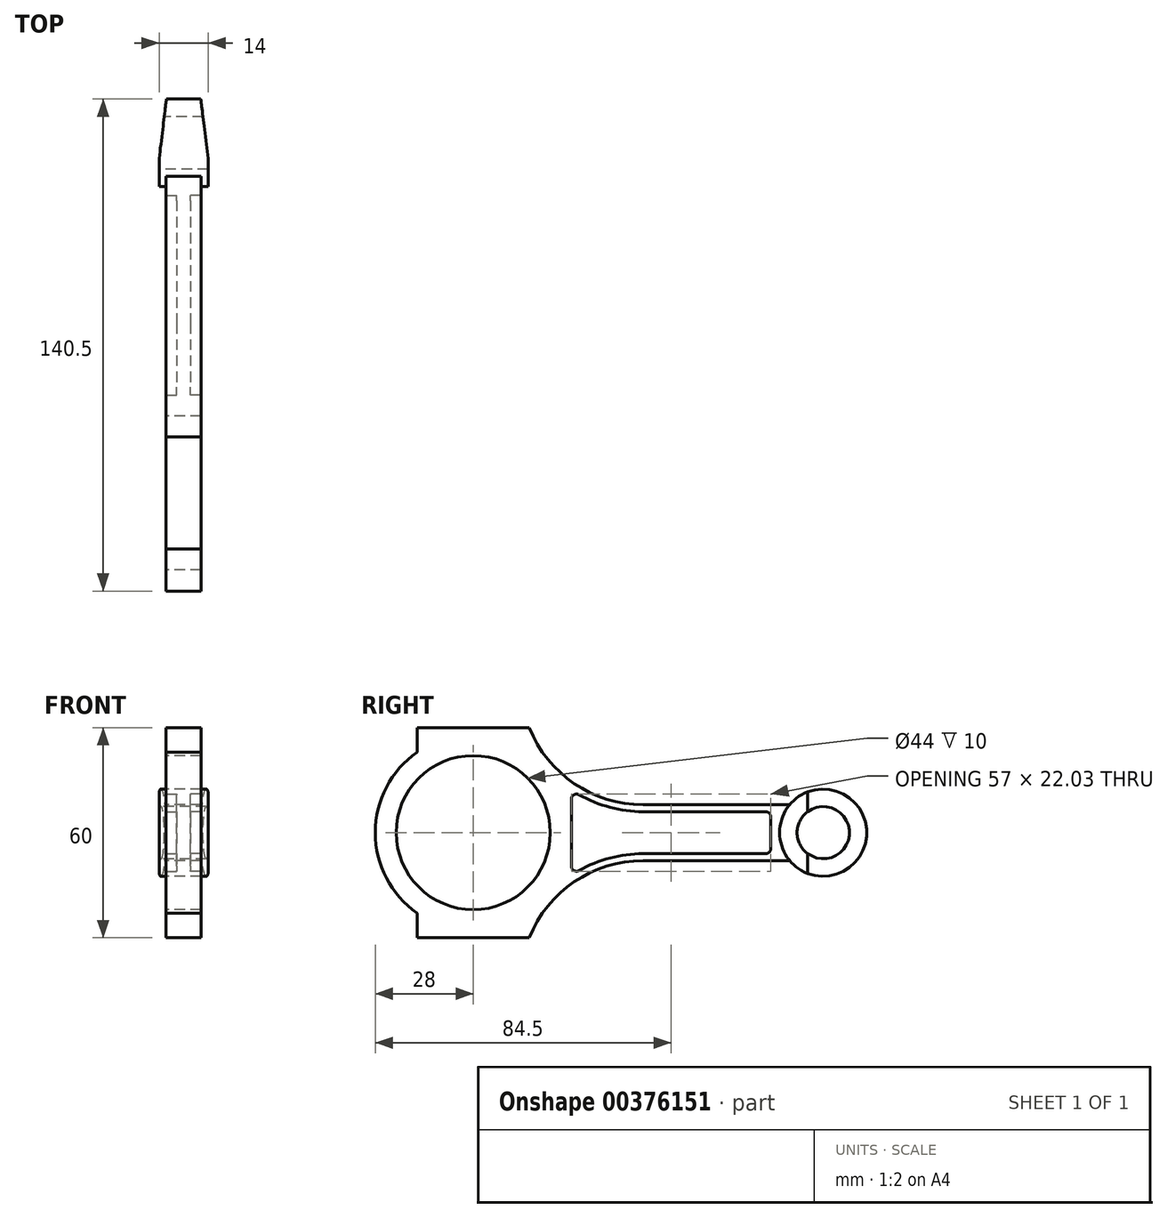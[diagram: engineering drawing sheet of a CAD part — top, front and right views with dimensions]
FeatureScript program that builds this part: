
annotation { "Feature Type Name" : "Feature", "Feature Type Description" : "" }
export const myFeature = defineFeature(function(context is Context, id is Id, definition is map)
    precondition{}
    {
        {
            var Q0;
            Q0=qCreatedBy(makeId("Right.planeOp"),FACE);
            var sketch = newSketch(context, id + "F0", { "sketchPlane" : qUnion([Q0])});
            skArc(sketch, "E0", {"start": v(-20, 0) * mm, "mid": v(0, -20) * mm, "end": v(20, 0) * mm});
            skArc(sketch, "E1", {"start": v(92.5, 0) * mm, "mid": v(100, -7.5) * mm, "end": v(107.5, 0) * mm});
            skArc(sketch, "E2", {"start": v(-22, 0) * mm, "mid": v(0, -22) * mm, "end": v(22, 0) * mm});
            skArc(sketch, "E3", {"start": v(87.5, 0) * mm, "mid": v(100, -12.5) * mm, "end": v(112.5, 0) * mm});
            skLineSegment(sketch, "E4", {"start": v(90.4, -8) * mm, "end": v(48.5, -8) * mm});
            skLineSegment(sketch, "E5", {"start": v(-22, 0) * mm, "end": v(112.5, 0) * mm, "construction": true});
            skLineSegment(sketch, "E6", {"start": v(-16, -30) * mm, "end": v(16, -30) * mm});
            skLineSegment(sketch, "E7", {"start": v(112.5, 0) * mm, "end": v(107.5, 0) * mm});
            skLineSegment(sketch, "E8", {"start": v(92.5, 0) * mm, "end": v(87.5, 0) * mm});
            skArc(sketch, "E9", {"start": v(16, -30) * mm, "mid": v(28.87, -14.02) * mm, "end": v(48.5, -8) * mm});
            skLineSegment(sketch, "E10", {"start": v(-16, -30) * mm, "end": v(-16, -22.98) * mm});
            skArc(sketch, "E11", {"start": v(-28, 0) * mm, "mid": v(-24.82, -12.96) * mm, "end": v(-16, -22.98) * mm});
            skLineSegment(sketch, "E12", {"start": v(-28, 0) * mm, "end": v(-22, 0) * mm});
            skLineSegment(sketch, "E13", {"start": v(22, 0) * mm, "end": v(87.5, 0) * mm});
            skLineSegment(sketch, "E14", {"start": v(85, 0) * mm, "end": v(85, -4.5) * mm});
            skLineSegment(sketch, "E15", {"start": v(83.5, -6) * mm, "end": v(48.5, -6) * mm});
            skArc(sketch, "E16.0", {"start": v(30.24, -10.82) * mm, "mid": v(39.06, -7.22) * mm, "end": v(48.5, -6) * mm});
            skLineSegment(sketch, "E17", {"start": v(28, -9.51) * mm, "end": v(28, 0) * mm});
            skPoint(sketch, "E17.endSnap0", {"position": v(45.25, 0) * mm});
            skPoint(sketch, "E18.visualSharp", {"position": v(28, -12.2) * mm});
            skArc(sketch, "E18.filletArc", {"start": v(28, -9.51) * mm, "mid": v(28.75, -10.8) * mm, "end": v(30.24, -10.82) * mm});
            skPoint(sketch, "E19.visualSharp", {"position": v(85, -6) * mm});
            skArc(sketch, "E19.filletArc", {"start": v(83.5, -6) * mm, "mid": v(84.56, -5.56) * mm, "end": v(85, -4.5) * mm});
            skSolve(sketch);
        }
        {
            var Q0;
            Q0=makeQuery(id+"F0.imprint","IMPRINT",FACE,{"disambiguationData":[TD([[makeQuery(id+"F0.imprint","IMPRINT",EDGE,{"derivedFrom":sQuery(id+"F0.wireOp",EDGE,"E1")}),-1.0]])]});
            extrude(context, id + "F1", {"entities" : qUnion([Q0]), "depth" : 7 * mm});
        }
        {
            var Q0;
            Q0=makeQuery(id+"F0.imprint","IMPRINT",FACE,{"disambiguationData":[TD([[makeQuery(id+"F0.imprint","IMPRINT",EDGE,{"derivedFrom":sQuery(id+"F0.wireOp",EDGE,"E2")}),-1.0]])]});
            extrude(context, id + "F2", {"entities" : qUnion([Q0]), "operationType" : NewBodyOperationType.ADD, "depth" : 5 * mm});
        }
        {
            var Q0;
            {var subQ0=sQuery(id+"F0.wireOp",EDGE,"E14");Q0=makeQuery(id+"F0.imprint","IMPRINT",FACE,{"disambiguationData":[TD([[makeQuery(id+"F0.imprint","IMPRINT",EDGE,{"derivedFrom":subQ0}),-1.0]])]});}
            extrude(context, id + "F3", {"entities" : qUnion([Q0]), "operationType" : NewBodyOperationType.ADD, "depth" : 2 * mm});
        }
        {
            var Q0;
            Q0=makeQuery(id+"F1.opExtrude","SWEPT_BODY",BODY,{"disambiguationData":[OSD([sQuery(id+"F0.wireOp",EDGE,"E1"),sQuery(id+"F0.wireOp",EDGE,"E3"),sQuery(id+"F0.wireOp",EDGE,"E7"),sQuery(id+"F0.wireOp",EDGE,"E8")])]});
            var Q1;
            Q1=qCreatedBy(makeId("Right.planeOp"),FACE);
            mirror(context, id + "F4", {"operationType" : NewBodyOperationType.ADD, "entities" : qUnion([Q0]), "mirrorPlane" : qUnion([Q1])});
        }
        {
            var Q0;
            Q0=makeQuery(id+"F1.opExtrude","SWEPT_BODY",BODY,{"disambiguationData":[OSD([sQuery(id+"F0.wireOp",EDGE,"E1"),sQuery(id+"F0.wireOp",EDGE,"E3"),sQuery(id+"F0.wireOp",EDGE,"E7"),sQuery(id+"F0.wireOp",EDGE,"E8")])]});
            var Q1;
            Q1=qCreatedBy(makeId("Top.planeOp"),FACE);
            mirror(context, id + "F5", {"operationType" : NewBodyOperationType.ADD, "entities" : qUnion([Q0]), "mirrorPlane" : qUnion([Q1])});
        }
        {
            var Q0;
            Q0=qCreatedBy(makeId("Top.planeOp"),FACE);
            var sketch = newSketch(context, id + "F6", { "sketchPlane" : qUnion([Q0])});
            skLineSegment(sketch, "E20", {"start": v(-7, 95.5) * mm, "end": v(-4.91, 112.5) * mm});
            skLineSegment(sketch, "E21", {"start": v(-7, 112.5) * mm, "end": v(-4.91, 112.5) * mm});
            skLineSegment(sketch, "E22", {"start": v(0, 119.54) * mm, "end": v(0, 168.64) * mm, "construction": true});
            skLineSegment(sketch, "E23", {"start": v(-7, 95.5) * mm, "end": v(-7, 112.5) * mm});
            skLineSegment(sketch, "E24.MirrorCS", {"start": v(7, 95.5) * mm, "end": v(4.91, 112.5) * mm});
            skLineSegment(sketch, "E25.MirrorCS", {"start": v(7, 95.5) * mm, "end": v(7, 112.5) * mm});
            skLineSegment(sketch, "E26.MirrorCS", {"start": v(7, 112.5) * mm, "end": v(4.91, 112.5) * mm});
            skSolve(sketch);
        }
        {
            var Q0;
            Q0=makeQuery(id+"F6.imprint","IMPRINT",FACE,{"disambiguationData":[TD([[makeQuery(id+"F6.imprint","IMPRINT",EDGE,{"derivedFrom":sQuery(id+"F6.wireOp",EDGE,"E20")}),1.0]])]});
            var Q1;
            Q1=makeQuery(id+"F6.imprint","IMPRINT",FACE,{"disambiguationData":[TD([[makeQuery(id+"F6.imprint","IMPRINT",EDGE,{"derivedFrom":sQuery(id+"F6.wireOp",EDGE,"E24.MirrorCS")}),-1.0]])]});
            extrude(context, id + "F7", {"entities" : qUnion([Q0, Q1]), "operationType" : NewBodyOperationType.REMOVE, "endBound" : BoundingType.SYMMETRIC, "oppositeDirection" : true, "depth" : 50 * mm});
        }
    });
